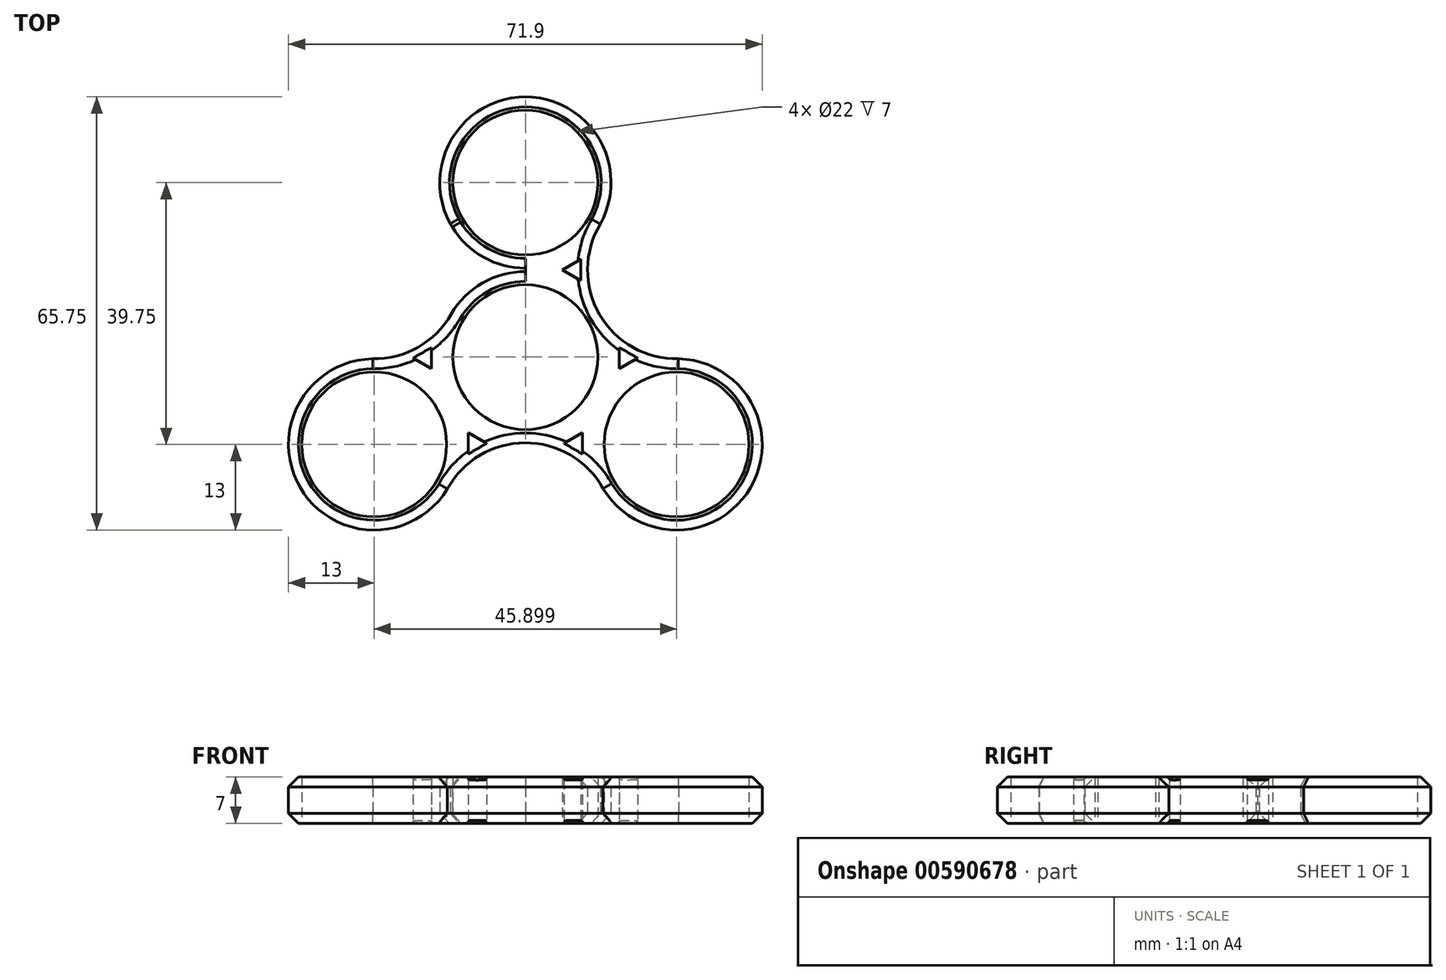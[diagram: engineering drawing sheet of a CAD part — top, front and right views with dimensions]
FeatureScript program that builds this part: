
annotation { "Feature Type Name" : "Feature", "Feature Type Description" : "" }
export const myFeature = defineFeature(function(context is Context, id is Id, definition is map)
    precondition{}
    {
        {
            var Q0;
            Q0=qCreatedBy(makeId("Top.planeOp"),FACE);
            var sketch = newSketch(context, id + "F0", { "sketchPlane" : qUnion([Q0])});
            skCircle(sketch, "E0", {"center": v(0, 0) * mm, "radius": 11 * mm});
            skCircle(sketch, "E1", {"center": v(0, 26.5) * mm, "radius": 11 * mm});
            skCircle(sketch, "E2.0", {"center": v(0, 26.5) * mm, "radius": 13 * mm});
            skLineSegment(sketch, "E3", {"start": v(9.53, 5.5) * mm, "end": v(22.52, 13) * mm});
            skLineSegment(sketch, "E4", {"start": v(22.52, 13) * mm, "end": v(15.77, 24.7) * mm});
            skLineSegment(sketch, "E5.MirrorCS", {"start": v(22.52, 13) * mm, "end": v(29.27, 1.3) * mm});
            skCircle(sketch, "E6.0", {"center": v(0, 0) * mm, "radius": 13 * mm});
            skPoint(sketch, "E7", {"position": v(11.26, 6.5) * mm});
            skArc(sketch, "E8", {"start": v(11.37, 20.2) * mm, "mid": v(13.15, 3.96) * mm, "end": v(29.27, 1.3) * mm});
            skLineSegment(sketch, "E9", {"start": v(11.15, 19.81) * mm, "end": v(11.15, 19.81) * mm});
            skCircle(sketch, "E10.1.0", {"center": v(-22.95, -13.25) * mm, "radius": 13 * mm});
            skCircle(sketch, "E10.1.1", {"center": v(-22.95, -13.25) * mm, "radius": 11 * mm});
            skArc(sketch, "E10.1.2", {"start": v(-23.17, -0.25) * mm, "mid": v(-10, 9.41) * mm, "end": v(-15.77, 24.7) * mm});
            skCircle(sketch, "E10.2.0", {"center": v(22.95, -13.25) * mm, "radius": 13 * mm});
            skCircle(sketch, "E10.2.1", {"center": v(22.95, -13.25) * mm, "radius": 11 * mm});
            skArc(sketch, "E10.2.2", {"start": v(11.8, -19.94) * mm, "mid": v(-3.15, -13.37) * mm, "end": v(-13.5, -26) * mm});
            skLineSegment(sketch, "E11", {"start": v(0, 11) * mm, "end": v(0, 15.5) * mm});
            skLineSegment(sketch, "E12", {"start": v(0, 15.5) * mm, "end": v(0, 13.25) * mm});
            skLineSegment(sketch, "E13.0", {"start": v(-5.6, 13.25) * mm, "end": v(-8.4, 14.87) * mm});
            skLineSegment(sketch, "E13.1", {"start": v(-5.6, 13.25) * mm, "end": v(-8.4, 11.63) * mm});
            skLineSegment(sketch, "E13.2", {"start": v(-8.4, 11.63) * mm, "end": v(-8.4, 14.87) * mm});
            skLineSegment(sketch, "E14.MirrorCS", {"start": v(5.6, 13.25) * mm, "end": v(8.4, 14.87) * mm});
            skLineSegment(sketch, "E15.MirrorCS", {"start": v(5.6, 13.25) * mm, "end": v(8.4, 11.63) * mm});
            skLineSegment(sketch, "E16.MirrorCS", {"start": v(8.4, 11.63) * mm, "end": v(8.4, 14.87) * mm});
            skLineSegment(sketch, "E17.1.0", {"start": v(-14.28, -1.77) * mm, "end": v(-17.07, -0.16) * mm});
            skLineSegment(sketch, "E17.1.1", {"start": v(-14.28, -1.77) * mm, "end": v(-14.28, 1.46) * mm});
            skLineSegment(sketch, "E17.1.2", {"start": v(-14.28, 1.46) * mm, "end": v(-17.07, -0.16) * mm});
            skLineSegment(sketch, "E17.1.3", {"start": v(-8.67, -11.48) * mm, "end": v(-8.67, -14.7) * mm});
            skLineSegment(sketch, "E17.1.4", {"start": v(-5.88, -13.1) * mm, "end": v(-8.67, -14.7) * mm});
            skLineSegment(sketch, "E17.1.5", {"start": v(-8.67, -11.48) * mm, "end": v(-5.88, -13.1) * mm});
            skLineSegment(sketch, "E17.2.0", {"start": v(8.67, -11.48) * mm, "end": v(8.67, -14.7) * mm});
            skLineSegment(sketch, "E17.2.1", {"start": v(8.67, -11.48) * mm, "end": v(5.88, -13.1) * mm});
            skLineSegment(sketch, "E17.2.2", {"start": v(5.88, -13.1) * mm, "end": v(8.67, -14.7) * mm});
            skLineSegment(sketch, "E17.2.3", {"start": v(14.28, -1.77) * mm, "end": v(17.07, -0.16) * mm});
            skLineSegment(sketch, "E17.2.4", {"start": v(14.28, 1.46) * mm, "end": v(17.07, -0.16) * mm});
            skLineSegment(sketch, "E17.2.5", {"start": v(14.28, -1.77) * mm, "end": v(14.28, 1.46) * mm});
            skSolve(sketch);
        }
        {
            var Q0;
            Q0=makeQuery(id+"F0.imprint","IMPRINT",FACE,{"disambiguationData":[TD([[makeQuery(id+"F0.imprint","IMPRINT",EDGE,{"derivedFrom":sQuery(id+"F0.wireOp",EDGE,"E1")}),-1.0]])]});
            var Q1;
            {var subQ3=sQuery(id+"F0.wireOp",EDGE,"E2.0");var subQ5=sQuery(id+"F0.wireOp",EDGE,"E10.1.2");var subQ6=makeQuery(id+"F0.imprint","INTERSECT",VERTEX,{"disambiguationData":[OD(1.0)],"derivedFrom":[subQ3,subQ5]});Q1=makeQuery(id+"F0.imprint","IMPRINT",FACE,{"disambiguationData":[TD([[makeQuery(id+"F0.imprint","IMPRINT",EDGE,{"disambiguationData":[TD([[subQ6,-1.0]])],"derivedFrom":subQ3}),-1.0]])]});}
            var Q2;
            {var subQ1=sQuery(id+"F0.wireOp",EDGE,"58c8e942-58a0-4348-91f7-dfcd7700a5c80.MirrorCS");var subQ3=sQuery(id+"F0.wireOp",EDGE,"E10.1.2");var subQ4=makeQuery(id+"F0.imprint","INTERSECT",VERTEX,{"derivedFrom":[subQ1,subQ3]});Q2=makeQuery(id+"F0.imprint","IMPRINT",FACE,{"disambiguationData":[TD([[makeQuery(id+"F0.imprint","IMPRINT",EDGE,{"disambiguationData":[TD([[subQ4,1.0]])],"derivedFrom":subQ3}),-1.0]])]});}
            var Q3;
            Q3=makeQuery(id+"F0.imprint","IMPRINT",FACE,{"disambiguationData":[TD([[makeQuery(id+"F0.imprint","IMPRINT",EDGE,{"derivedFrom":sQuery(id+"F0.wireOp",EDGE,"E0")}),-1.0]])]});
            var Q4;
            {var subQ1=sQuery(id+"F0.wireOp",EDGE,"NzhgkqC9-E64v-pG9t-CCg1-1XiLNCIsjjtQ");var subQ3=sQuery(id+"F0.wireOp",EDGE,"E8");var subQ4=makeQuery(id+"F0.imprint","INTERSECT",VERTEX,{"derivedFrom":[subQ1,subQ3]});Q4=makeQuery(id+"F0.imprint","IMPRINT",FACE,{"disambiguationData":[TD([[makeQuery(id+"F0.imprint","IMPRINT",EDGE,{"disambiguationData":[TD([[subQ4,1.0]])],"derivedFrom":subQ1}),-1.0]])]});}
            var Q5;
            {var subQ0=sQuery(id+"F0.wireOp",EDGE,"E10.2.2");var subQ5=sQuery(id+"F0.wireOp",EDGE,"E10.2.0");var subQ7=makeQuery(id+"F0.imprint","INTERSECT",VERTEX,{"disambiguationData":[OD(1.0)],"derivedFrom":[subQ5,subQ0]});Q5=makeQuery(id+"F0.imprint","IMPRINT",FACE,{"disambiguationData":[TD([[makeQuery(id+"F0.imprint","IMPRINT",EDGE,{"disambiguationData":[TD([[subQ7,1.0]])],"derivedFrom":subQ5}),-1.0]])]});}
            var Q6;
            Q6=makeQuery(id+"F0.imprint","IMPRINT",FACE,{"disambiguationData":[TD([[makeQuery(id+"F0.imprint","IMPRINT",EDGE,{"derivedFrom":sQuery(id+"F0.wireOp",EDGE,"E10.2.1")}),-1.0]])]});
            var Q7;
            {var subQ0=sQuery(id+"F0.wireOp",EDGE,"E10.1.2");var subQ1=sQuery(id+"F0.wireOp",EDGE,"E6.0");var subQ2=makeQuery(id+"F0.imprint","INTERSECT",VERTEX,{"derivedFrom":[subQ1,subQ0]});Q7=makeQuery(id+"F0.imprint","IMPRINT",FACE,{"disambiguationData":[TD([[makeQuery(id+"F0.imprint","IMPRINT",EDGE,{"disambiguationData":[TD([[subQ2,-1.0]])],"derivedFrom":subQ1}),-1.0]])]});}
            var Q8;
            Q8=makeQuery(id+"F0.imprint","IMPRINT",FACE,{"disambiguationData":[TD([[makeQuery(id+"F0.imprint","IMPRINT",EDGE,{"derivedFrom":sQuery(id+"F0.wireOp",EDGE,"E10.1.1")}),-1.0]])]});
            var Q9;
            Q9=makeQuery(id+"F0.imprint","IMPRINT",FACE,{"disambiguationData":[TD([[makeQuery(id+"F0.imprint","IMPRINT",EDGE,{"derivedFrom":sQuery(id+"F0.wireOp",EDGE,"E14.MirrorCS")}),1.0]])]});
            var Q10;
            {var subQ4=sQuery(id+"F0.wireOp",EDGE,"E3");var subQ5=sQuery(id+"F0.wireOp",EDGE,"E0");var subQ6=makeQuery(id+"F0.imprint","INTERSECT",VERTEX,{"derivedFrom":[subQ5,subQ4]});Q10=makeQuery(id+"F0.imprint","IMPRINT",FACE,{"disambiguationData":[TD([[makeQuery(id+"F0.imprint","IMPRINT",EDGE,{"disambiguationData":[TD([[subQ6,1.0]])],"derivedFrom":subQ5}),-1.0]])]});}
            extrude(context, id + "F1", {"entities" : qUnion([Q0, Q1, Q2, Q3, Q4, Q5, Q6, Q7, Q8, Q9, Q10]), "depth" : 7 * mm, "offsetDistance" : 25 * mm});
        }
        {
            var Q0;
            Q0=makeQuery(id+"F1.opExtrude","CAP_EDGE",EDGE,{"disambiguationData":[OSD([sQuery(id+"F0.wireOp",EDGE,"E10.1.2")])],"isStart":false});
            var Q1;
            Q1=makeQuery(id+"F1.opExtrude","CAP_EDGE",EDGE,{"disambiguationData":[OSD([sQuery(id+"F0.wireOp",EDGE,"E2.0")])],"isStart":false});
            var Q2;
            Q2=makeQuery(id+"F1.opExtrude","CAP_EDGE",EDGE,{"disambiguationData":[OSD([sQuery(id+"F0.wireOp",EDGE,"E8")])],"isStart":false});
            var Q3;
            Q3=makeQuery(id+"F1.opExtrude","CAP_EDGE",EDGE,{"disambiguationData":[OSD([sQuery(id+"F0.wireOp",EDGE,"E10.2.0")])],"isStart":false});
            var Q4;
            Q4=makeQuery(id+"F1.opExtrude","CAP_EDGE",EDGE,{"disambiguationData":[OSD([sQuery(id+"F0.wireOp",EDGE,"E10.2.2")])],"isStart":false});
            var Q5;
            Q5=makeQuery(id+"F1.opExtrude","CAP_EDGE",EDGE,{"disambiguationData":[OSD([sQuery(id+"F0.wireOp",EDGE,"E10.1.0")])],"isStart":false});
            var Q6;
            Q6=makeQuery(id+"F1.opExtrude","CAP_EDGE",EDGE,{"disambiguationData":[OSD([sQuery(id+"F0.wireOp",EDGE,"E8")])],"isStart":true});
            var Q7;
            Q7=makeQuery(id+"F1.opExtrude","CAP_EDGE",EDGE,{"disambiguationData":[OSD([sQuery(id+"F0.wireOp",EDGE,"E2.0")])],"isStart":true});
            var Q8;
            Q8=makeQuery(id+"F1.opExtrude","CAP_EDGE",EDGE,{"disambiguationData":[OSD([sQuery(id+"F0.wireOp",EDGE,"E10.1.2")])],"isStart":true});
            var Q9;
            Q9=makeQuery(id+"F1.opExtrude","CAP_EDGE",EDGE,{"disambiguationData":[OSD([sQuery(id+"F0.wireOp",EDGE,"E10.1.0")])],"isStart":true});
            var Q10;
            Q10=makeQuery(id+"F1.opExtrude","CAP_EDGE",EDGE,{"disambiguationData":[OSD([sQuery(id+"F0.wireOp",EDGE,"E10.2.2")])],"isStart":true});
            var Q11;
            Q11=makeQuery(id+"F1.opExtrude","CAP_EDGE",EDGE,{"disambiguationData":[OSD([sQuery(id+"F0.wireOp",EDGE,"E10.2.0")])],"isStart":true});
            chamfer(context, id + "F2", {"entities" : qUnion([Q0, Q1, Q2, Q3, Q4, Q5, Q6, Q7, Q8, Q9, Q10, Q11]), "width" : 1.5 * mm, "tangentPropagation" : true});
        }
    });
